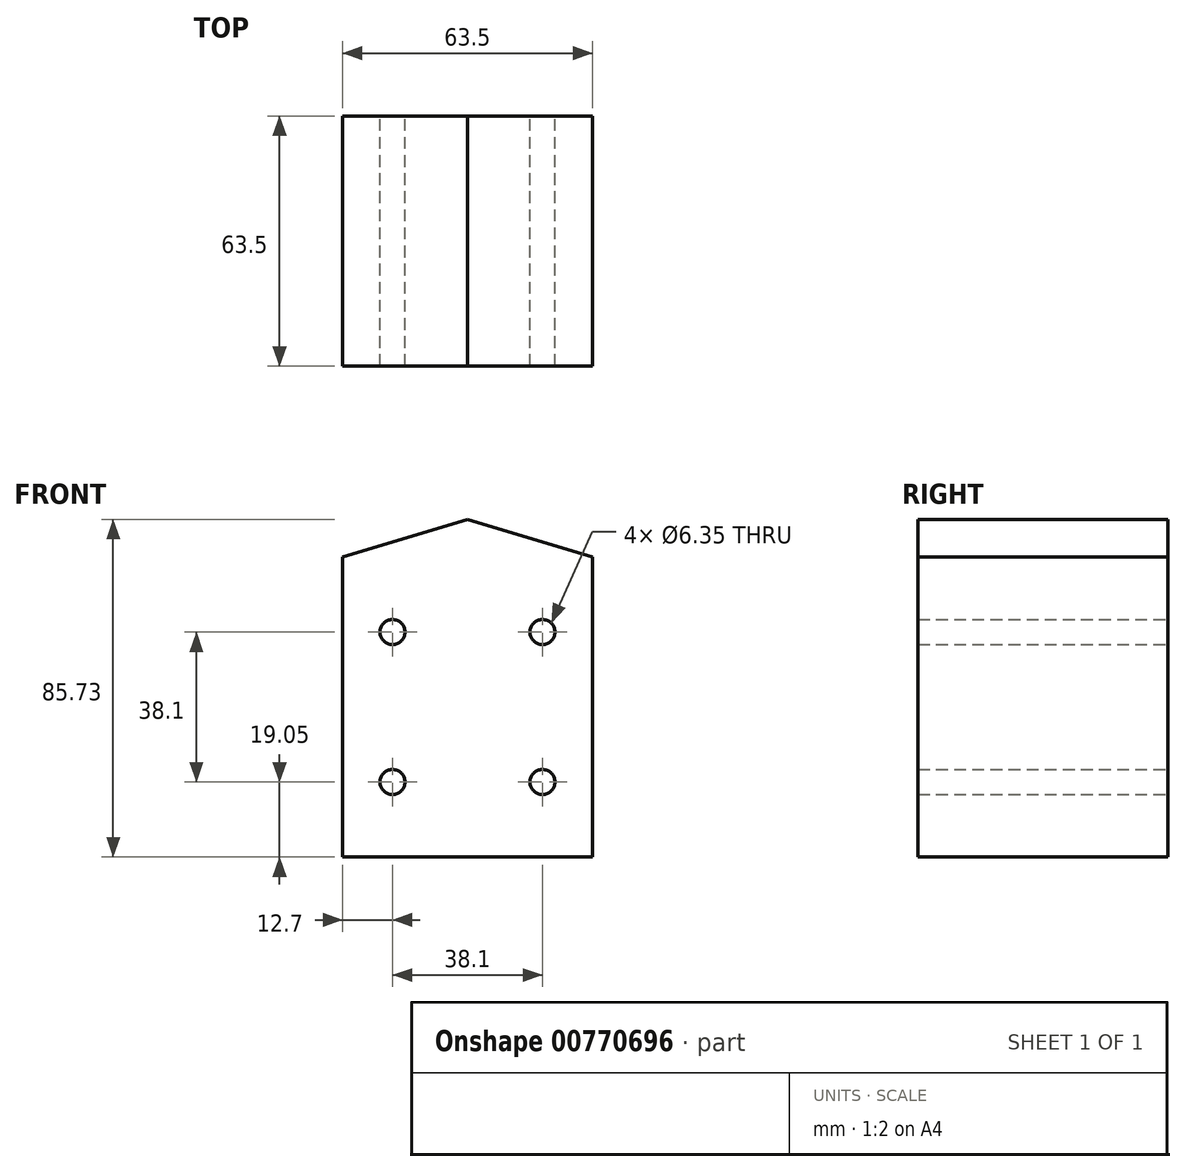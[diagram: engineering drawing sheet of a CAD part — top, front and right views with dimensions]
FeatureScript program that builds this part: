
annotation { "Feature Type Name" : "Feature", "Feature Type Description" : "" }
export const myFeature = defineFeature(function(context is Context, id is Id, definition is map)
    precondition{}
    {
        {
            var Q0;
            Q0=qCreatedBy(makeId("Front.planeOp"),FACE);
            var sketch = newSketch(context, id + "F0", { "sketchPlane" : qUnion([Q0])});
            skLineSegment(sketch, "E0.bottom", {"start": v(-31.75, -38.1) * mm, "end": v(31.75, -38.1) * mm});
            skLineSegment(sketch, "E0.top", {"start": v(-31.75, 38.1) * mm, "end": v(31.75, 38.1) * mm});
            skLineSegment(sketch, "E0.left", {"start": v(-31.75, -38.1) * mm, "end": v(-31.75, 38.1) * mm});
            skLineSegment(sketch, "E0.right", {"start": v(31.75, -38.1) * mm, "end": v(31.75, 38.1) * mm});
            skPoint(sketch, "E0.middle", {"position": v(0, 0) * mm});
            skSolve(sketch);
        }
        {
            var Q0;
            Q0 = qSketchRegion(id + "F0", true);
            extrude(context, id + "F1", {"entities" : qUnion([Q0]), "endBound" : BoundingType.SYMMETRIC, "depth" : 63.5 * mm, "offsetDistance" : 25.4 * mm});
        }
        {
            var Q0;
            Q0=makeQuery(id+"F1.opExtrude","CAP_FACE",FACE,{"disambiguationData":[OSD([sQuery(id+"F0.wireOp",EDGE,"E0.bottom"),sQuery(id+"F0.wireOp",EDGE,"E0.top"),sQuery(id+"F0.wireOp",EDGE,"E0.left"),sQuery(id+"F0.wireOp",EDGE,"E0.right")])],"isStart":false});
            var sketch = newSketch(context, id + "F2", { "sketchPlane" : qUnion([Q0])});
            skLineSegment(sketch, "E1", {"start": v(-31.75, 38.1) * mm, "end": v(0, 47.62) * mm});
            skLineSegment(sketch, "E2", {"start": v(0, 47.62) * mm, "end": v(31.75, 38.1) * mm});
            skLineSegment(sketch, "E3", {"start": v(31.75, 38.1) * mm, "end": v(-31.75, 38.1) * mm});
            skLineSegment(sketch, "E4", {"start": v(0, 47.62) * mm, "end": v(0, 38.1) * mm, "construction": true});
            skSolve(sketch);
        }
        {
            var Q0;
            Q0 = qSketchRegion(id + "F2", true);
            var Q1;
            Q1=makeQuery(id+"F1.opExtrude","CAP_FACE",FACE,{"disambiguationData":[OSD([sQuery(id+"F0.wireOp",EDGE,"E0.bottom"),sQuery(id+"F0.wireOp",EDGE,"E0.top"),sQuery(id+"F0.wireOp",EDGE,"E0.left"),sQuery(id+"F0.wireOp",EDGE,"E0.right")])],"isStart":true});
            extrude(context, id + "F3", {"entities" : qUnion([Q0]), "operationType" : NewBodyOperationType.ADD, "endBound" : BoundingType.UP_TO_SURFACE, "oppositeDirection" : true, "depth" : 25.4 * mm, "endBoundEntityFace" : qUnion([Q1]), "offsetDistance" : 25.4 * mm});
        }
        {
            var Q0;
            {var subQ0=sQuery(id+"F0.wireOp",EDGE,"E0.right");var subQ1=sQuery(id+"F0.wireOp",EDGE,"E0.left");var subQ2=sQuery(id+"F0.wireOp",EDGE,"E0.top");var subQ3=sQuery(id+"F0.wireOp",EDGE,"E0.bottom");Q0=makeQuery(id+"F3.boolean.opBoolean","MERGE",FACE,{"derivedFrom":[makeQuery(id+"F1.opExtrude","CAP_FACE",FACE,{"disambiguationData":[OSD([subQ3,subQ2,subQ1,subQ0])],"isStart":true}),makeQuery(id+"F3.opExtrude","CAP_FACE",FACE,{"disambiguationData":[OSD([subQ3,subQ2,subQ1,subQ0])],"isStart":false})]});}
            var sketch = newSketch(context, id + "F4", { "sketchPlane" : qUnion([Q0])});
            skLineSegment(sketch, "E5.bottom", {"start": v(19.05, -19.05) * mm, "end": v(-19.05, -19.05) * mm});
            skLineSegment(sketch, "E5.top", {"start": v(19.05, 19.05) * mm, "end": v(-19.05, 19.05) * mm});
            skLineSegment(sketch, "E5.left", {"start": v(19.05, -19.05) * mm, "end": v(19.05, 19.05) * mm});
            skLineSegment(sketch, "E5.right", {"start": v(-19.05, -19.05) * mm, "end": v(-19.05, 19.05) * mm});
            skPoint(sketch, "E5.middle", {"position": v(0, 0) * mm});
            skSolve(sketch);
        }
        {
            var Q0;
            Q0=sQuery(id+"F4.wireOp",VERTEX,"E5.top.end");
            var Q1;
            Q1=sQuery(id+"F4.wireOp",VERTEX,"E5.top.start");
            var Q2;
            Q2=sQuery(id+"F4.wireOp",VERTEX,"E5.bottom.end");
            var Q3;
            Q3=sQuery(id+"F4.wireOp",VERTEX,"E5.bottom.start");
            var Q4;
            Q4=makeQuery(id+"F1.opExtrude","SWEPT_BODY",BODY,{"disambiguationData":[OSD([sQuery(id+"F0.wireOp",EDGE,"E0.bottom"),sQuery(id+"F0.wireOp",EDGE,"E0.top"),sQuery(id+"F0.wireOp",EDGE,"E0.left"),sQuery(id+"F0.wireOp",EDGE,"E0.right")])]});
            hole(context, id + "F5", {"style" : HoleStyle.SIMPLE, "endStyle" : HoleEndStyle.THROUGH, "holeDiameter" : 6.35 * mm, "majorDiameter" : 6.35 * mm, "isTappedThrough" : true, "tappedDepth" : 12.7 * mm, "tapClearance" : 3, "locations" : qUnion([Q0, Q1, Q2, Q3]), "scope" : qUnion([Q4])});
        }
    });
